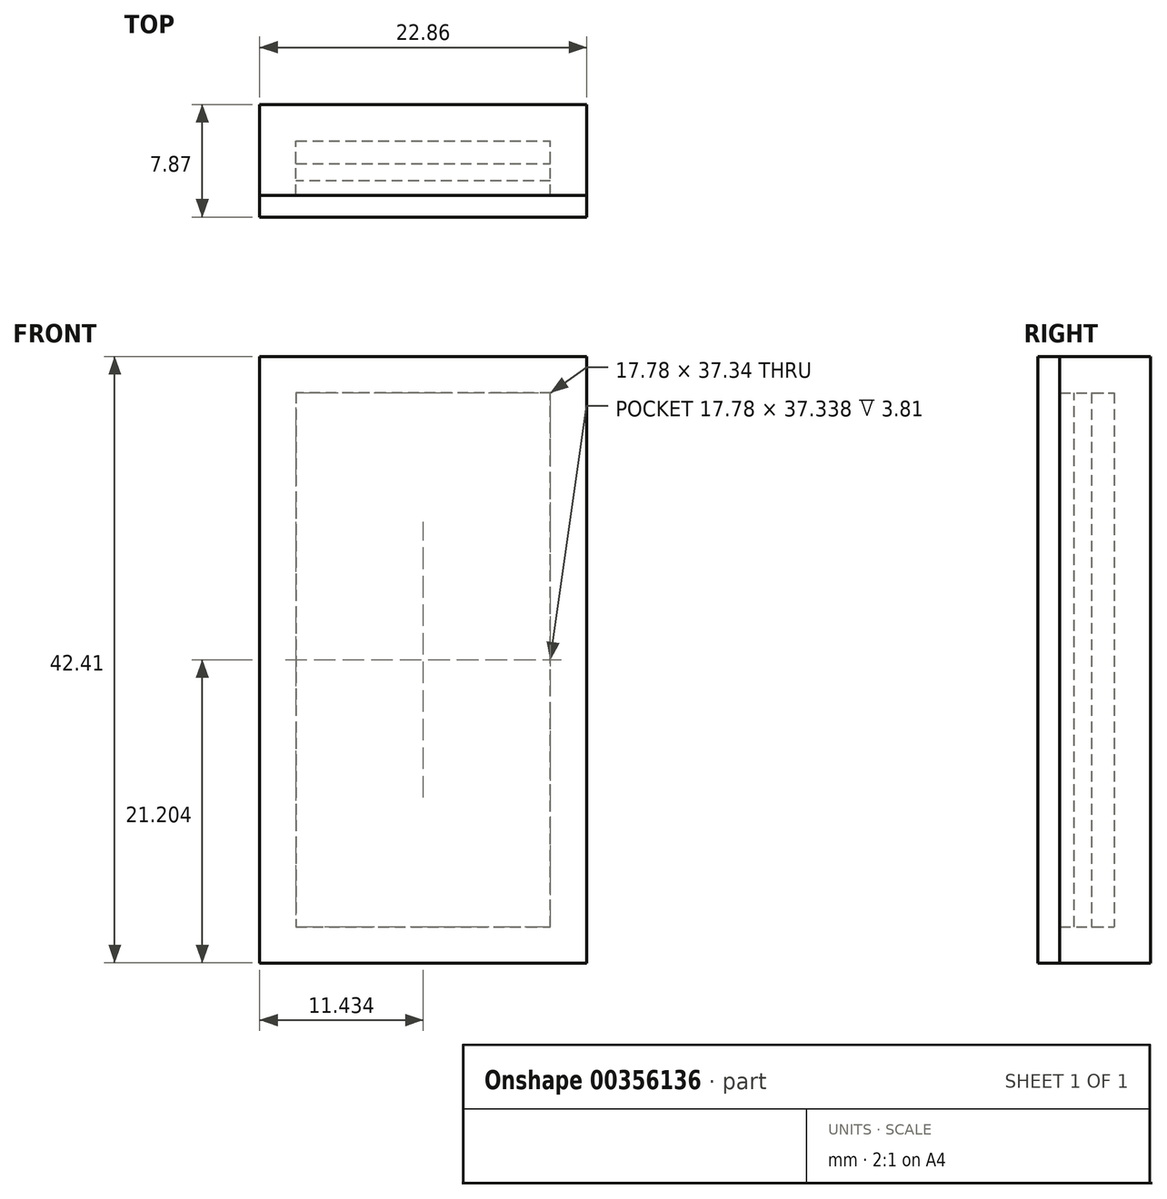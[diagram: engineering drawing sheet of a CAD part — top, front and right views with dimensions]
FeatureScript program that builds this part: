
annotation { "Feature Type Name" : "Feature", "Feature Type Description" : "" }
export const myFeature = defineFeature(function(context is Context, id is Id, definition is map)
    precondition{}
    {
        {
            var Q0;
            Q0=qCreatedBy(makeId("Front.planeOp"),FACE);
            var sketch = newSketch(context, id + "F0", { "sketchPlane" : qUnion([Q0])});
            skLineSegment(sketch, "E0.bottom", {"start": v(-9.14, 18.71) * mm, "end": v(8.64, 18.71) * mm});
            skLineSegment(sketch, "E0.top", {"start": v(-9.14, -18.62) * mm, "end": v(8.64, -18.62) * mm});
            skLineSegment(sketch, "E0.left", {"start": v(-9.14, 18.71) * mm, "end": v(-9.14, -18.62) * mm});
            skLineSegment(sketch, "E0.right", {"start": v(8.64, 18.71) * mm, "end": v(8.64, -18.62) * mm});
            skSolve(sketch);
        }
        {
            var Q0;
            Q0=makeQuery(id+"F0.imprint","IMPRINT",FACE,{"disambiguationData":[TD([[makeQuery(id+"F0.imprint","IMPRINT",EDGE,{"derivedFrom":sQuery(id+"F0.wireOp",EDGE,"E0.bottom")}),-1.0]])]});
            extrude(context, id + "F1", {"entities" : qUnion([Q0]), "depth" : 1.59 * mm});
        }
        {
            var Q0;
            Q0=makeQuery(id+"F1.opExtrude","CAP_FACE",FACE,{"disambiguationData":[OSD([sQuery(id+"F0.wireOp",EDGE,"E0.bottom"),sQuery(id+"F0.wireOp",EDGE,"E0.top"),sQuery(id+"F0.wireOp",EDGE,"E0.left"),sQuery(id+"F0.wireOp",EDGE,"E0.right")])],"isStart":true});
            cPlane(context, id + "F2", {"entities" : qUnion([Q0]), "cplaneType" : CPlaneType.OFFSET, "offset" : 2.54 * mm, "width" : 152.4 * mm, "height" : 152.4 * mm});
        }
        {
            var Q0;
            Q0=qCreatedBy(id+"F2.planeOp",FACE);
            var sketch = newSketch(context, id + "F3", { "sketchPlane" : qUnion([Q0])});
            skLineSegment(sketch, "E1.0", {"start": v(11.68, 21.25) * mm, "end": v(-11.18, 21.25) * mm});
            skLineSegment(sketch, "E1.1", {"start": v(11.68, 21.25) * mm, "end": v(11.68, -21.16) * mm});
            skLineSegment(sketch, "E1.2", {"start": v(11.68, -21.16) * mm, "end": v(-11.18, -21.16) * mm});
            skLineSegment(sketch, "E1.3", {"start": v(-11.18, 21.25) * mm, "end": v(-11.18, -21.16) * mm});
            skSolve(sketch);
        }
        {
            var Q0;
            Q0=makeQuery(id+"F3.imprint","IMPRINT",FACE,{"disambiguationData":[TD([[makeQuery(id+"F3.imprint","IMPRINT",EDGE,{"derivedFrom":sQuery(id+"F3.wireOp",EDGE,"E1.0")}),1.0]])]});
            extrude(context, id + "F4", {"entities" : qUnion([Q0]), "oppositeDirection" : true, "depth" : 6.35 * mm});
        }
        {
            var Q0;
            Q0=makeQuery(id+"F4.opExtrude","CAP_FACE",FACE,{"disambiguationData":[OSD([sQuery(id+"F3.wireOp",EDGE,"E1.0"),sQuery(id+"F3.wireOp",EDGE,"E1.1"),sQuery(id+"F3.wireOp",EDGE,"E1.2"),sQuery(id+"F3.wireOp",EDGE,"E1.3")])],"isStart":false});
            shell(context, id + "F5", {"entities" : qUnion([Q0]), "thickness" : 2.54 * mm});
        }
        {
            var Q0;
            Q0=makeQuery(id+"F4.opExtrude","CAP_FACE",FACE,{"disambiguationData":[OSD([sQuery(id+"F3.wireOp",EDGE,"E1.0"),sQuery(id+"F3.wireOp",EDGE,"E1.1"),sQuery(id+"F3.wireOp",EDGE,"E1.2"),sQuery(id+"F3.wireOp",EDGE,"E1.3")])],"isStart":false});
            cPlane(context, id + "F6", {"entities" : qUnion([Q0]), "cplaneType" : CPlaneType.OFFSET, "offset" : 1.02 * mm, "oppositeDirection" : true, "width" : 152.4 * mm, "height" : 152.4 * mm});
        }
        {
            var Q0;
            Q0=qCreatedBy(id+"F6.planeOp",FACE);
            var sketch = newSketch(context, id + "F7", { "sketchPlane" : qUnion([Q0])});
            skLineSegment(sketch, "E2.0", {"start": v(-11.68, 21.25) * mm, "end": v(11.18, 21.25) * mm});
            skLineSegment(sketch, "E3.0", {"start": v(11.18, 21.25) * mm, "end": v(11.18, -21.16) * mm});
            skLineSegment(sketch, "E4.0", {"start": v(-11.68, 21.25) * mm, "end": v(-11.68, -21.16) * mm});
            skLineSegment(sketch, "E5.0", {"start": v(-11.68, -21.16) * mm, "end": v(11.18, -21.16) * mm});
            skSolve(sketch);
        }
        {
            var Q0;
            Q0 = qSketchRegion(id + "F7", true);
            extrude(context, id + "F8", {"entities" : qUnion([Q0]), "depth" : 2.54 * mm});
        }
        {
            var Q0;
            Q0=makeQuery(id+"F4.opExtrude","SWEPT_BODY",BODY,{"disambiguationData":[OSD([sQuery(id+"F3.wireOp",EDGE,"E1.0"),sQuery(id+"F3.wireOp",EDGE,"E1.1"),sQuery(id+"F3.wireOp",EDGE,"E1.2"),sQuery(id+"F3.wireOp",EDGE,"E1.3")])]});
            var Q1;
            Q1=makeQuery(id+"F8.opExtrude","SWEPT_BODY",BODY,{"disambiguationData":[OSD([sQuery(id+"F7.wireOp",EDGE,"E2.0"),sQuery(id+"F7.wireOp",EDGE,"E3.0"),sQuery(id+"F7.wireOp",EDGE,"E4.0"),sQuery(id+"F7.wireOp",EDGE,"E5.0")])]});
            booleanBodies(context, id + "F9", {"operationType" : BooleanOperationType.SUBTRACTION, "tools" : qUnion([Q0]), "targets" : qUnion([Q1]), "keepTools" : true});
        }
    });
